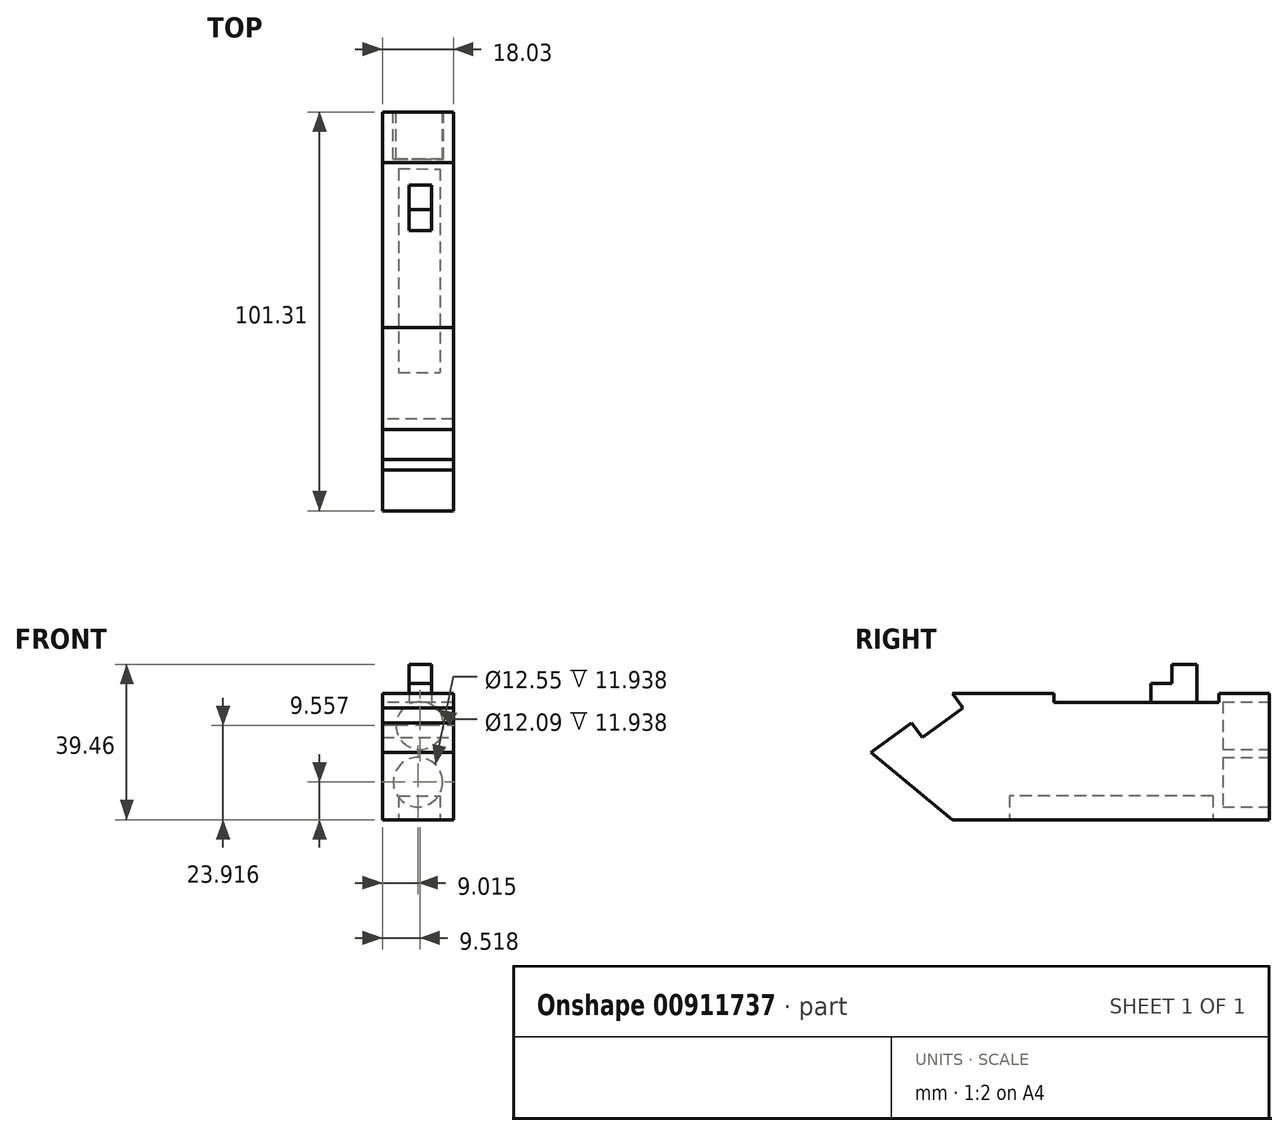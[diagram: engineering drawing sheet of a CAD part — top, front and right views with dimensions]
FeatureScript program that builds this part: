
annotation { "Feature Type Name" : "Feature", "Feature Type Description" : "" }
export const myFeature = defineFeature(function(context is Context, id is Id, definition is map)
    precondition{}
    {
        {
            var Q0;
            Q0=qCreatedBy(makeId("Right.planeOp"),FACE);
            var sketch = newSketch(context, id + "F0", { "sketchPlane" : qUnion([Q0])});
            skLineSegment(sketch, "E0.bottom", {"start": v(-41.3, 32.1) * mm, "end": v(39.29, 32.1) * mm});
            skLineSegment(sketch, "E0.top", {"start": v(-41.3, 0) * mm, "end": v(39.29, 0) * mm});
            skLineSegment(sketch, "E0.right", {"start": v(39.29, 32.1) * mm, "end": v(39.29, 0) * mm});
            skLineSegment(sketch, "E1", {"start": v(-41.3, 32.1) * mm, "end": v(-62.02, 17.12) * mm});
            skLineSegment(sketch, "E2", {"start": v(-62.02, 17.12) * mm, "end": v(-41.3, 0) * mm});
            skSolve(sketch);
        }
        {
            var Q0;
            Q0=makeQuery(id+"F0.imprint","IMPRINT",FACE,{"disambiguationData":[TD([[makeQuery(id+"F0.imprint","IMPRINT",EDGE,{"derivedFrom":sQuery(id+"F0.wireOp",EDGE,"E0.bottom")}),-1.0]])]});
            extrude(context, id + "F1", {"entities" : qUnion([Q0]), "depth" : 18.03 * mm, "offsetDistance" : 25.4 * mm});
        }
        {
            var Q0;
            Q0=makeQuery(id+"F1.opExtrude","SWEPT_FACE",FACE,{"disambiguationData":[OSD([sQuery(id+"F0.wireOp",EDGE,"E0.right")])]});
            var sketch = newSketch(context, id + "F2", { "sketchPlane" : qUnion([Q0])});
            skCircle(sketch, "E3", {"center": v(-9.52, 23.92) * mm, "radius": 6.05 * mm});
            skCircle(sketch, "E4", {"center": v(-9.01, 9.56) * mm, "radius": 6.28 * mm});
            skSolve(sketch);
        }
        {
            var Q0;
            Q0=makeQuery(id+"F2.imprint","IMPRINT",FACE,{"disambiguationData":[TD([[makeQuery(id+"F2.imprint","IMPRINT",EDGE,{"derivedFrom":sQuery(id+"F2.wireOp",EDGE,"E3")}),1.0]])]});
            var Q1;
            Q1=makeQuery(id+"F2.imprint","IMPRINT",FACE,{"disambiguationData":[TD([[makeQuery(id+"F2.imprint","IMPRINT",EDGE,{"derivedFrom":sQuery(id+"F2.wireOp",EDGE,"E4")}),1.0]])]});
            extrude(context, id + "F3", {"entities" : qUnion([Q0, Q1]), "operationType" : NewBodyOperationType.REMOVE, "oppositeDirection" : true, "depth" : 11.94 * mm, "offsetDistance" : 25.4 * mm});
        }
        {
            var Q0;
            Q0=makeQuery(id+"F1.opExtrude","SWEPT_FACE",FACE,{"disambiguationData":[OSD([sQuery(id+"F0.wireOp",EDGE,"E1")])]});
            var sketch = newSketch(context, id + "F4", { "sketchPlane" : qUnion([Q0])});
            skLineSegment(sketch, "E5.bottom", {"start": v(0, -14.7) * mm, "end": v(18.03, -14.7) * mm});
            skLineSegment(sketch, "E5.top", {"start": v(0, -27.47) * mm, "end": v(18.03, -27.47) * mm});
            skLineSegment(sketch, "E5.left", {"start": v(0, -14.7) * mm, "end": v(0, -27.47) * mm});
            skLineSegment(sketch, "E5.right", {"start": v(18.03, -14.7) * mm, "end": v(18.03, -27.47) * mm});
            skSolve(sketch);
        }
        {
            var Q0;
            Q0=makeQuery(id+"F4.imprint","IMPRINT",FACE,{"disambiguationData":[TD([[makeQuery(id+"F4.imprint","IMPRINT",EDGE,{"derivedFrom":sQuery(id+"F4.wireOp",EDGE,"E5.bottom")}),1.0]])]});
            extrude(context, id + "F5", {"entities" : qUnion([Q0]), "operationType" : NewBodyOperationType.REMOVE, "oppositeDirection" : true, "depth" : 4.57 * mm, "offsetDistance" : 25.4 * mm});
        }
        {
            var Q0;
            Q0=makeQuery(id+"F1.opExtrude","SWEPT_FACE",FACE,{"disambiguationData":[OSD([sQuery(id+"F0.wireOp",EDGE,"E0.top")])]});
            var sketch = newSketch(context, id + "F6", { "sketchPlane" : qUnion([Q0])});
            skLineSegment(sketch, "E6.bottom", {"start": v(4.04, -24.9) * mm, "end": v(14.65, -24.87) * mm});
            skLineSegment(sketch, "E7.top", {"start": v(4.04, 26.88) * mm, "end": v(14.65, 26.88) * mm});
            skLineSegment(sketch, "E8", {"start": v(4.04, -24.9) * mm, "end": v(4.04, 26.88) * mm});
            skLineSegment(sketch, "E9", {"start": v(14.65, -24.87) * mm, "end": v(14.65, 26.88) * mm});
            skSolve(sketch);
        }
        {
            var Q0;
            Q0=makeQuery(id+"F6.imprint","IMPRINT",FACE,{"disambiguationData":[TD([[makeQuery(id+"F6.imprint","IMPRINT",EDGE,{"derivedFrom":sQuery(id+"F6.wireOp",EDGE,"E6.bottom")}),1.0]])]});
            extrude(context, id + "F7", {"entities" : qUnion([Q0]), "operationType" : NewBodyOperationType.REMOVE, "oppositeDirection" : true, "depth" : 6.1 * mm, "offsetDistance" : 25.4 * mm});
        }
        {
            var Q0;
            Q0=makeQuery(id+"F1.opExtrude","SWEPT_FACE",FACE,{"disambiguationData":[OSD([sQuery(id+"F0.wireOp",EDGE,"E0.bottom")])]});
            var sketch = newSketch(context, id + "F8", { "sketchPlane" : qUnion([Q0])});
            skLineSegment(sketch, "E10.bottom", {"start": v(18.03, -15.46) * mm, "end": v(0, -15.46) * mm});
            skLineSegment(sketch, "E10.top", {"start": v(18.03, 26.42) * mm, "end": v(0, 26.42) * mm});
            skLineSegment(sketch, "E10.left", {"start": v(18.03, -15.46) * mm, "end": v(18.03, 26.42) * mm});
            skLineSegment(sketch, "E10.right", {"start": v(0, -15.46) * mm, "end": v(0, 26.42) * mm});
            skSolve(sketch);
        }
        {
            var Q0;
            Q0=makeQuery(id+"F8.imprint","IMPRINT",FACE,{"disambiguationData":[TD([[makeQuery(id+"F8.imprint","IMPRINT",EDGE,{"derivedFrom":sQuery(id+"F8.wireOp",EDGE,"E10.bottom")}),-1.0]])]});
            extrude(context, id + "F9", {"entities" : qUnion([Q0]), "operationType" : NewBodyOperationType.REMOVE, "oppositeDirection" : true, "depth" : 2.3 * mm, "offsetDistance" : 25.4 * mm});
        }
        {
            var Q0;
            Q0=makeQuery(id+"F9.boolean.opBoolean","COPY",FACE,{"derivedFrom":makeQuery(id+"F9.opExtrude","CAP_FACE",FACE,{"disambiguationData":[OSD([sQuery(id+"F8.wireOp",EDGE,"E10.bottom"),sQuery(id+"F8.wireOp",EDGE,"E10.top"),sQuery(id+"F8.wireOp",EDGE,"E10.left"),sQuery(id+"F8.wireOp",EDGE,"E10.right")])],"isStart":false})});
            var sketch = newSketch(context, id + "F10", { "sketchPlane" : qUnion([Q0])});
            skLineSegment(sketch, "E11.bottom", {"start": v(12.41, 20.8) * mm, "end": v(6.77, 20.8) * mm});
            skLineSegment(sketch, "E11.top", {"start": v(12.41, 14.5) * mm, "end": v(6.77, 14.5) * mm});
            skLineSegment(sketch, "E11.left", {"start": v(12.41, 20.8) * mm, "end": v(12.41, 14.5) * mm});
            skLineSegment(sketch, "E11.right", {"start": v(6.77, 20.8) * mm, "end": v(6.77, 14.5) * mm});
            skSolve(sketch);
        }
        {
            var Q0;
            Q0 = qSketchRegion(id + "F10", true);
            extrude(context, id + "F11", {"entities" : qUnion([Q0]), "operationType" : NewBodyOperationType.ADD, "depth" : 9.65 * mm, "offsetDistance" : 25.4 * mm});
        }
        {
            var Q0;
            Q0=makeQuery(id+"F11.opExtrude","SWEPT_FACE",FACE,{"disambiguationData":[OSD([sQuery(id+"F10.wireOp",EDGE,"E11.top")])]});
            var sketch = newSketch(context, id + "F12", { "sketchPlane" : qUnion([Q0])});
            skLineSegment(sketch, "E12.bottom", {"start": v(6.77, 34.63) * mm, "end": v(12.41, 34.63) * mm});
            skLineSegment(sketch, "E12.top", {"start": v(6.77, 29.8) * mm, "end": v(12.41, 29.8) * mm});
            skLineSegment(sketch, "E12.left", {"start": v(6.77, 34.63) * mm, "end": v(6.77, 29.8) * mm});
            skLineSegment(sketch, "E12.right", {"start": v(12.41, 34.63) * mm, "end": v(12.41, 29.8) * mm});
            skSolve(sketch);
        }
        {
            var Q0;
            Q0=makeQuery(id+"F12.imprint","IMPRINT",FACE,{"disambiguationData":[TD([[makeQuery(id+"F12.imprint","IMPRINT",EDGE,{"derivedFrom":sQuery(id+"F12.wireOp",EDGE,"E12.bottom")}),-1.0]])]});
            extrude(context, id + "F13", {"entities" : qUnion([Q0]), "operationType" : NewBodyOperationType.ADD, "depth" : 5.33 * mm, "offsetDistance" : 25.4 * mm});
        }
    });
